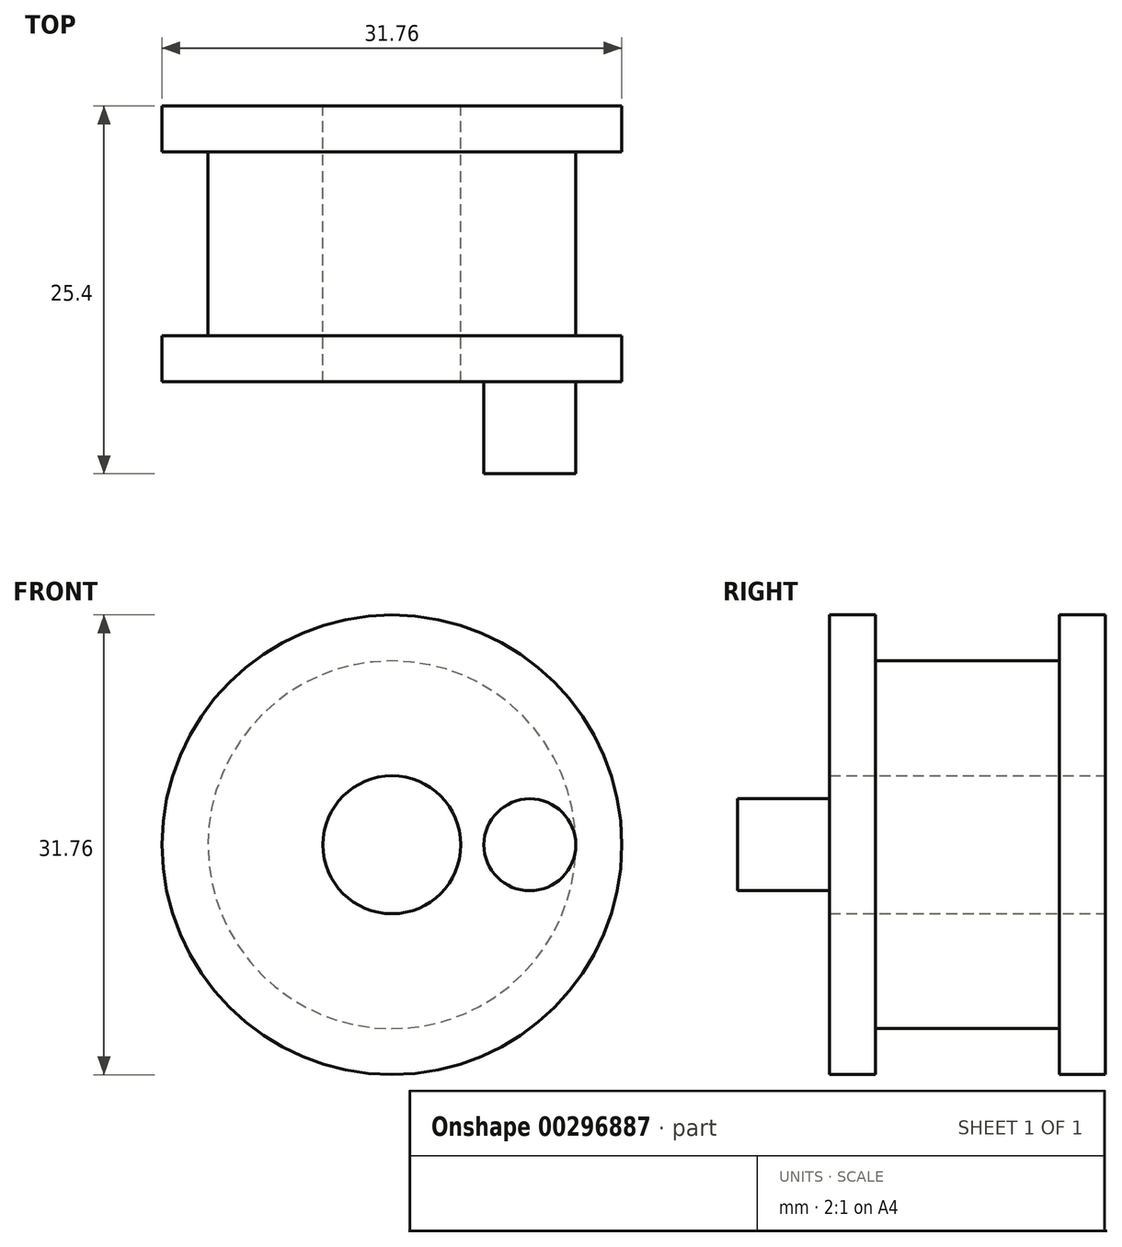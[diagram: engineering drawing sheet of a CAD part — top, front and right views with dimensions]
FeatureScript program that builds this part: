
annotation { "Feature Type Name" : "Feature", "Feature Type Description" : "" }
export const myFeature = defineFeature(function(context is Context, id is Id, definition is map)
    precondition{}
    {
        {
            var Q0;
            Q0=qCreatedBy(makeId("Right.planeOp"),FACE);
            var sketch = newSketch(context, id + "F0", { "sketchPlane" : qUnion([Q0])});
            skLineSegment(sketch, "E0", {"start": v(0, 0) * mm, "end": v(0, 4.76) * mm});
            skLineSegment(sketch, "E1", {"start": v(0, 4.76) * mm, "end": v(-19.05, 4.76) * mm});
            skLineSegment(sketch, "E2", {"start": v(-19.05, 4.76) * mm, "end": v(-19.05, 15.87) * mm});
            skLineSegment(sketch, "E3", {"start": v(-19.05, 15.87) * mm, "end": v(-15.87, 15.87) * mm});
            skLineSegment(sketch, "E4", {"start": v(-15.87, 15.88) * mm, "end": v(-15.87, 12.7) * mm});
            skLineSegment(sketch, "E5", {"start": v(-15.88, 12.7) * mm, "end": v(-3.17, 12.7) * mm});
            skLineSegment(sketch, "E6", {"start": v(-3.17, 12.7) * mm, "end": v(-3.18, 15.88) * mm});
            skLineSegment(sketch, "E7", {"start": v(-3.17, 15.88) * mm, "end": v(0, 15.88) * mm});
            skLineSegment(sketch, "E8", {"start": v(0, 15.88) * mm, "end": v(0, 4.76) * mm});
            skLineSegment(sketch, "E9", {"start": v(0, 0) * mm, "end": v(-21.2, 0) * mm});
            skSolve(sketch);
        }
        {
            var Q0;
            Q0=makeQuery(id+"F0.imprint","IMPRINT",FACE,{"disambiguationData":[TD([[makeQuery(id+"F0.imprint","IMPRINT",EDGE,{"derivedFrom":sQuery(id+"F0.wireOp",EDGE,"E1")}),-1.0]])]});
            var Q1;
            Q1=sQuery(id+"F0.wireOp",EDGE,"E9");
            revolve(context, id + "F1", {"entities" : qUnion([Q0]), "axis" : qUnion([Q1]), "revolveType" : RevolveType.FULL});
        }
        {
            var Q0;
            Q0=makeQuery(id+"F1.opRevolve","SWEPT_FACE",FACE,{"disambiguationData":[OSD([sQuery(id+"F0.wireOp",EDGE,"E2")])]});
            var sketch = newSketch(context, id + "F2", { "sketchPlane" : qUnion([Q0])});
            skLineSegment(sketch, "E10", {"start": v(0, 0) * mm, "end": v(9.53, 0) * mm});
            skCircle(sketch, "E11", {"center": v(9.53, 0) * mm, "radius": 3.18 * mm});
            skSolve(sketch);
        }
        {
            var Q0;
            Q0=qSketchRegion(id+"F2",true);
            extrude(context, id + "F3", {"entities" : qUnion([Q0]), "operationType" : NewBodyOperationType.ADD, "depth" : 6.35 * mm});
        }
    });
